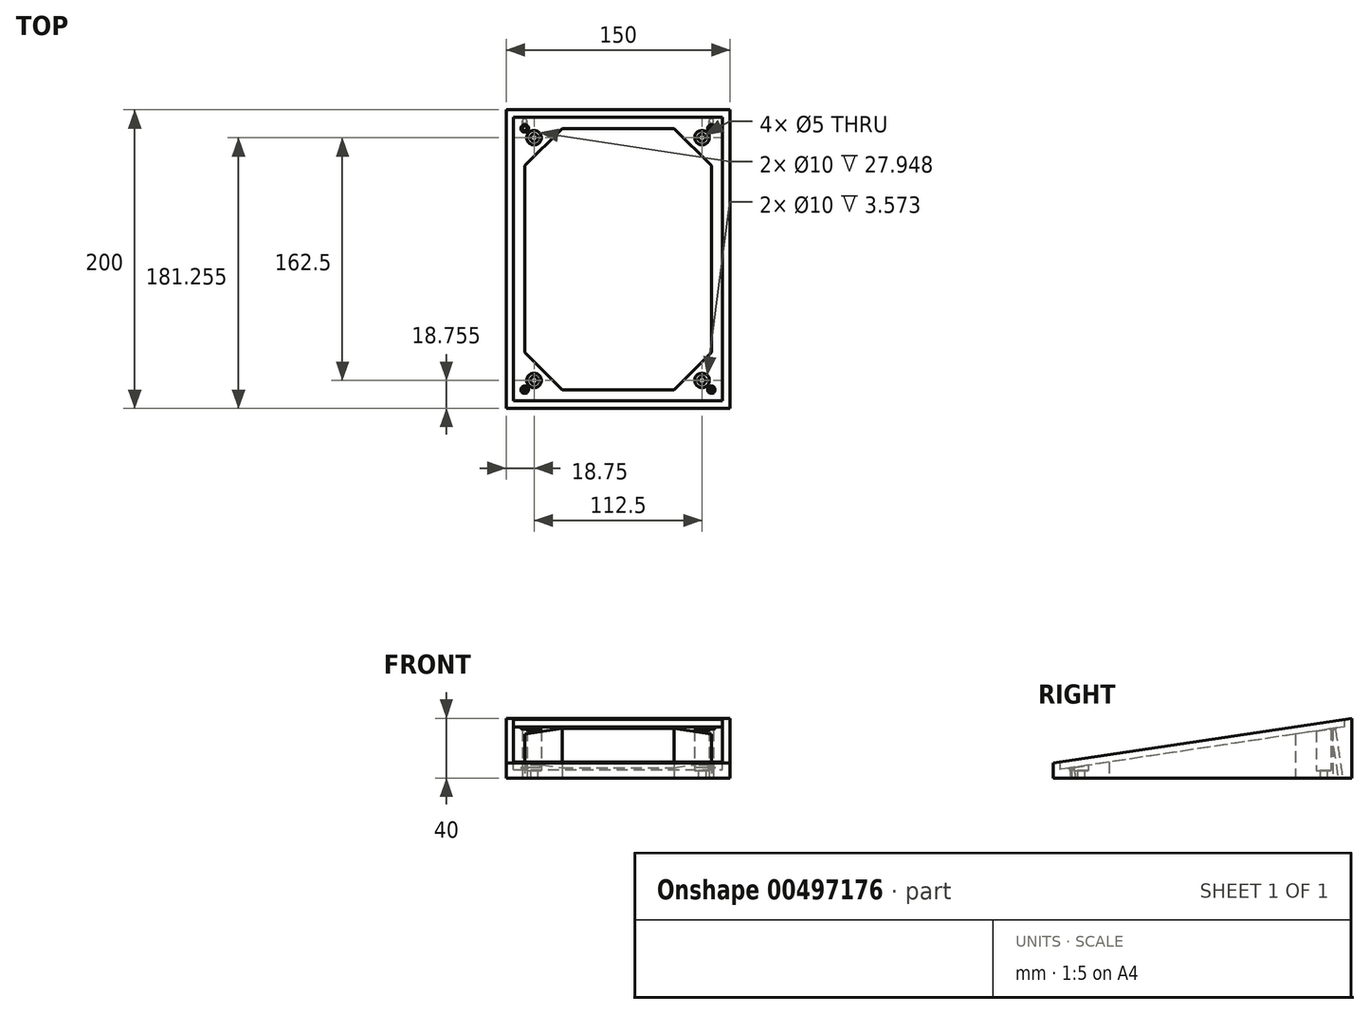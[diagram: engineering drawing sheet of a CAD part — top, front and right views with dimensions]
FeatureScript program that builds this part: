
annotation { "Feature Type Name" : "Feature", "Feature Type Description" : "" }
export const myFeature = defineFeature(function(context is Context, id is Id, definition is map)
    precondition{}
    {
        {
            var Q0;
            Q0=qCreatedBy(makeId("Top.planeOp"),FACE);
            var sketch = newSketch(context, id + "F0", { "sketchPlane" : qUnion([Q0])});
            skLineSegment(sketch, "E0.bottom", {"start": v(-75, 99.72) * mm, "end": v(75, 99.72) * mm});
            skLineSegment(sketch, "E0.top", {"start": v(-75, -100.28) * mm, "end": v(75, -100.28) * mm});
            skLineSegment(sketch, "E0.left", {"start": v(-75, 99.72) * mm, "end": v(-75, -100.28) * mm});
            skLineSegment(sketch, "E0.right", {"start": v(75, 99.72) * mm, "end": v(75, -100.28) * mm});
            skLineSegment(sketch, "E1.bottom", {"start": v(-68.75, 93.47) * mm, "end": v(68.75, 93.47) * mm});
            skLineSegment(sketch, "E1.top", {"start": v(-68.75, -94.03) * mm, "end": v(68.75, -94.03) * mm});
            skLineSegment(sketch, "E1.left", {"start": v(-68.75, 93.47) * mm, "end": v(-68.75, -94.03) * mm});
            skLineSegment(sketch, "E1.right", {"start": v(68.75, 93.47) * mm, "end": v(68.75, -94.03) * mm});
            skLineSegment(sketch, "E2.bottom", {"start": v(-62.5, 87.22) * mm, "end": v(62.5, 87.22) * mm});
            skLineSegment(sketch, "E2.top", {"start": v(-62.5, -87.78) * mm, "end": v(62.5, -87.78) * mm});
            skLineSegment(sketch, "E2.left", {"start": v(-62.5, 87.22) * mm, "end": v(-62.5, -87.78) * mm});
            skLineSegment(sketch, "E2.right", {"start": v(62.5, 87.22) * mm, "end": v(62.5, -87.78) * mm});
            skPoint(sketch, "E3", {"position": v(37.5, 87.22) * mm});
            skPoint(sketch, "E4", {"position": v(37.5, -87.78) * mm});
            skPoint(sketch, "E5", {"position": v(-37.5, 87.22) * mm});
            skPoint(sketch, "E6", {"position": v(-37.5, -87.78) * mm});
            skPoint(sketch, "E7", {"position": v(-62.5, 62.22) * mm});
            skPoint(sketch, "E8", {"position": v(62.5, 62.22) * mm});
            skPoint(sketch, "E9", {"position": v(62.5, -62.78) * mm});
            skPoint(sketch, "E10", {"position": v(-62.5, -62.78) * mm});
            skPoint(sketch, "E11", {"position": v(-62.5, 87.22) * mm});
            skPoint(sketch, "E12", {"position": v(62.5, 87.22) * mm});
            skPoint(sketch, "E13", {"position": v(62.5, -87.78) * mm});
            skPoint(sketch, "E14", {"position": v(-62.5, -87.78) * mm});
            skLineSegment(sketch, "E15", {"start": v(-62.5, -62.78) * mm, "end": v(-37.5, -87.78) * mm});
            skLineSegment(sketch, "E16", {"start": v(37.5, -87.78) * mm, "end": v(62.5, -62.78) * mm});
            skLineSegment(sketch, "E17", {"start": v(62.5, 62.22) * mm, "end": v(37.5, 87.22) * mm});
            skLineSegment(sketch, "E18", {"start": v(-37.5, 87.22) * mm, "end": v(-62.5, 62.22) * mm});
            skPoint(sketch, "E19", {"position": v(-50, 74.72) * mm});
            skPoint(sketch, "E20", {"position": v(50, 74.72) * mm});
            skPoint(sketch, "E21", {"position": v(50, -75.28) * mm});
            skPoint(sketch, "E22", {"position": v(-50, -75.28) * mm});
            skLineSegment(sketch, "E23", {"start": v(-62.5, 87.22) * mm, "end": v(-50, 74.72) * mm, "construction": true});
            skLineSegment(sketch, "E24", {"start": v(62.5, 87.22) * mm, "end": v(50, 74.72) * mm, "construction": true});
            skLineSegment(sketch, "E25", {"start": v(62.5, -87.78) * mm, "end": v(50, -75.28) * mm, "construction": true});
            skLineSegment(sketch, "E26", {"start": v(-62.5, -87.78) * mm, "end": v(-50, -75.28) * mm, "construction": true});
            skPoint(sketch, "E27", {"position": v(-56.25, 80.97) * mm});
            skPoint(sketch, "E28", {"position": v(56.25, 80.97) * mm});
            skPoint(sketch, "E29", {"position": v(56.25, -81.53) * mm});
            skPoint(sketch, "E30", {"position": v(-56.25, -81.53) * mm});
            skCircle(sketch, "E31", {"center": v(-56.25, -81.53) * mm, "radius": 2.5 * mm});
            skCircle(sketch, "E32", {"center": v(56.25, -81.53) * mm, "radius": 2.5 * mm});
            skCircle(sketch, "E33", {"center": v(56.25, 80.97) * mm, "radius": 2.5 * mm});
            skCircle(sketch, "E34", {"center": v(-56.25, 80.97) * mm, "radius": 2.5 * mm});
            skCircle(sketch, "E35", {"center": v(-56.25, 80.97) * mm, "radius": 5 * mm});
            skCircle(sketch, "E36", {"center": v(56.25, 80.97) * mm, "radius": 5 * mm});
            skCircle(sketch, "E37", {"center": v(-56.25, -81.53) * mm, "radius": 5 * mm});
            skCircle(sketch, "E38", {"center": v(56.25, -81.53) * mm, "radius": 5 * mm});
            skSolve(sketch);
        }
        {
            var Q0;
            Q0=makeQuery(id+"F0.imprint","IMPRINT",FACE,{"disambiguationData":[TD([[makeQuery(id+"F0.imprint","IMPRINT",EDGE,{"derivedFrom":sQuery(id+"F0.wireOp",EDGE,"E0.bottom")}),-1.0]])]});
            var Q1;
            Q1=makeQuery(id+"F0.imprint","IMPRINT",FACE,{"disambiguationData":[TD([[makeQuery(id+"F0.imprint","IMPRINT",EDGE,{"derivedFrom":sQuery(id+"F0.wireOp",EDGE,"E1.bottom")}),-1.0]])]});
            var Q2;
            {var subQ0=sQuery(id+"F0.wireOp",EDGE,"E17");Q2=makeQuery(id+"F0.imprint","IMPRINT",FACE,{"disambiguationData":[TD([[makeQuery(id+"F0.imprint","IMPRINT",EDGE,{"derivedFrom":subQ0}),-1.0]])]});}
            var Q3;
            {var subQ5=sQuery(id+"F0.wireOp",EDGE,"E18");Q3=makeQuery(id+"F0.imprint","IMPRINT",FACE,{"disambiguationData":[TD([[makeQuery(id+"F0.imprint","IMPRINT",EDGE,{"derivedFrom":subQ5}),-1.0]])]});}
            var Q4;
            {var subQ5=sQuery(id+"F0.wireOp",EDGE,"E15");Q4=makeQuery(id+"F0.imprint","IMPRINT",FACE,{"disambiguationData":[TD([[makeQuery(id+"F0.imprint","IMPRINT",EDGE,{"derivedFrom":subQ5}),-1.0]])]});}
            var Q5;
            {var subQ0=sQuery(id+"F0.wireOp",EDGE,"E16");Q5=makeQuery(id+"F0.imprint","IMPRINT",FACE,{"disambiguationData":[TD([[makeQuery(id+"F0.imprint","IMPRINT",EDGE,{"derivedFrom":subQ0}),-1.0]])]});}
            extrude(context, id + "F1", {"entities" : qUnion([Q0, Q1, Q2, Q3, Q4, Q5]), "depth" : 40 * mm});
        }
        {
            var Q0;
            Q0=makeQuery(id+"F1.opExtrude","SWEPT_FACE",FACE,{"disambiguationData":[OSD([sQuery(id+"F0.wireOp",EDGE,"E0.right")])]});
            var sketch = newSketch(context, id + "F2", { "sketchPlane" : qUnion([Q0])});
            skPoint(sketch, "E39", {"position": v(-100.28, 40) * mm});
            skPoint(sketch, "E40", {"position": v(99.72, 40) * mm});
            skPoint(sketch, "E41", {"position": v(-100.28, 10) * mm});
            skLineSegment(sketch, "E42", {"start": v(-100.28, 40) * mm, "end": v(99.72, 40) * mm});
            skLineSegment(sketch, "E43", {"start": v(-100.28, 40) * mm, "end": v(-100.28, 10) * mm});
            skLineSegment(sketch, "E44", {"start": v(-100.28, 10) * mm, "end": v(99.72, 40) * mm});
            skSolve(sketch);
        }
        {
            var Q0;
            Q0=makeQuery(id+"F2.imprint","IMPRINT",FACE,{"disambiguationData":[TD([[makeQuery(id+"F2.imprint","IMPRINT",EDGE,{"derivedFrom":sQuery(id+"F2.wireOp",EDGE,"E42")}),1.0]])]});
            extrude(context, id + "F3", {"entities" : qUnion([Q0]), "operationType" : NewBodyOperationType.REMOVE, "oppositeDirection" : true, "depth" : 155 * mm});
        }
        {
            var Q0;
            Q0=makeQuery(id+"F1.opExtrude","SWEPT_FACE",FACE,{"disambiguationData":[OSD([sQuery(id+"F0.wireOp",EDGE,"E0.right")])]});
            var sketch = newSketch(context, id + "F4", { "sketchPlane" : qUnion([Q0])});
            skPoint(sketch, "E45", {"position": v(94.72, 39.25) * mm});
            skPoint(sketch, "E46", {"position": v(99.72, 40) * mm});
            skPoint(sketch, "E47", {"position": v(-100.28, 10) * mm});
            skPoint(sketch, "E48", {"position": v(-95.28, 10.75) * mm});
            skPoint(sketch, "E49", {"position": v(-95.28, 5.75) * mm});
            skPoint(sketch, "E50", {"position": v(94.72, 34.25) * mm});
            skLineSegment(sketch, "E51", {"start": v(-95.28, 10.75) * mm, "end": v(94.72, 39.25) * mm});
            skLineSegment(sketch, "E52", {"start": v(94.72, 39.25) * mm, "end": v(94.72, 34.25) * mm});
            skLineSegment(sketch, "E53", {"start": v(94.72, 34.25) * mm, "end": v(-95.28, 5.75) * mm});
            skLineSegment(sketch, "E54", {"start": v(-95.28, 5.75) * mm, "end": v(-95.28, 10.75) * mm});
            skSolve(sketch);
        }
        {
            var Q0;
            Q0=makeQuery(id+"F4.imprint","IMPRINT",FACE,{"disambiguationData":[TD([[makeQuery(id+"F4.imprint","IMPRINT",EDGE,{"derivedFrom":sQuery(id+"F4.wireOp",EDGE,"E51")}),-1.0]])]});
            extrude(context, id + "F5", {"entities" : qUnion([Q0]), "operationType" : NewBodyOperationType.REMOVE, "oppositeDirection" : true, "depth" : 145 * mm, "hasSecondDirection" : true, "secondDirectionOppositeDirection" : true, "secondDirectionDepth" : 5 * mm});
        }
        {
            var Q0;
            Q0=makeQuery(id+"F0.imprint","IMPRINT",FACE,{"disambiguationData":[TD([[makeQuery(id+"F0.imprint","IMPRINT",EDGE,{"derivedFrom":sQuery(id+"F0.wireOp",EDGE,"E34")}),-1.0]])]});
            var Q1;
            Q1=makeQuery(id+"F0.imprint","IMPRINT",FACE,{"disambiguationData":[TD([[makeQuery(id+"F0.imprint","IMPRINT",EDGE,{"derivedFrom":sQuery(id+"F0.wireOp",EDGE,"E33")}),-1.0]])]});
            var Q2;
            Q2=makeQuery(id+"F0.imprint","IMPRINT",FACE,{"disambiguationData":[TD([[makeQuery(id+"F0.imprint","IMPRINT",EDGE,{"derivedFrom":sQuery(id+"F0.wireOp",EDGE,"E32")}),-1.0]])]});
            var Q3;
            Q3=makeQuery(id+"F0.imprint","IMPRINT",FACE,{"disambiguationData":[TD([[makeQuery(id+"F0.imprint","IMPRINT",EDGE,{"derivedFrom":sQuery(id+"F0.wireOp",EDGE,"E31")}),-1.0]])]});
            extrude(context, id + "F6", {"entities" : qUnion([Q0, Q1, Q2, Q3]), "operationType" : NewBodyOperationType.ADD, "depth" : 5 * mm});
        }
        {
            var Q0;
            Q0=makeQuery(id+"F5.boolean.opBoolean","COPY",FACE,{"derivedFrom":makeQuery(id+"F5.opExtrude","SWEPT_FACE",FACE,{"disambiguationData":[OSD([sQuery(id+"F4.wireOp",EDGE,"E53")])]})});
            var sketch = newSketch(context, id + "F7", { "sketchPlane" : qUnion([Q0])});
            skPoint(sketch, "E55", {"position": v(-56.25, 84.85) * mm});
            skPoint(sketch, "E56", {"position": v(56.25, 84.85) * mm});
            skPoint(sketch, "E57", {"position": v(56.25, -79.46) * mm});
            skPoint(sketch, "E58", {"position": v(-56.25, -79.46) * mm});
            skPoint(sketch, "E59", {"position": v(-62.5, 91.17) * mm});
            skPoint(sketch, "E60", {"position": v(62.5, 91.17) * mm});
            skPoint(sketch, "E61", {"position": v(62.5, -85.78) * mm});
            skPoint(sketch, "E62", {"position": v(-62.5, -85.78) * mm});
            skPoint(sketch, "E63", {"position": v(-70, -93.37) * mm});
            skPoint(sketch, "E64", {"position": v(-70, 98.76) * mm});
            skPoint(sketch, "E65", {"position": v(70, -93.37) * mm});
            skSolve(sketch);
        }
        {
            var Q0;
            Q0=sQuery(id+"F7.wireOp",VERTEX,"E62");
            var Q1;
            Q1=sQuery(id+"F7.wireOp",VERTEX,"E59");
            var Q2;
            Q2=sQuery(id+"F7.wireOp",VERTEX,"E60");
            var Q3;
            Q3=sQuery(id+"F7.wireOp",VERTEX,"E61");
            var Q4;
            Q4=makeQuery(id+"F1.opExtrude","SWEPT_BODY",BODY,{"disambiguationData":[OSD([sQuery(id+"F0.wireOp",EDGE,"E0.bottom"),sQuery(id+"F0.wireOp",EDGE,"E0.top"),sQuery(id+"F0.wireOp",EDGE,"E0.left"),sQuery(id+"F0.wireOp",EDGE,"E0.right"),sQuery(id+"F0.wireOp",EDGE,"E2.bottom"),sQuery(id+"F0.wireOp",EDGE,"E2.top"),sQuery(id+"F0.wireOp",EDGE,"E2.left"),sQuery(id+"F0.wireOp",EDGE,"E2.right"),sQuery(id+"F0.wireOp",EDGE,"E15"),sQuery(id+"F0.wireOp",EDGE,"E16"),sQuery(id+"F0.wireOp",EDGE,"E17"),sQuery(id+"F0.wireOp",EDGE,"E18"),sQuery(id+"F0.wireOp",EDGE,"E35"),sQuery(id+"F0.wireOp",EDGE,"E36"),sQuery(id+"F0.wireOp",EDGE,"E37"),sQuery(id+"F0.wireOp",EDGE,"E38")])]});
            hole(context, id + "F8", {"style" : HoleStyle.C_SINK, "endStyle" : HoleEndStyle.THROUGH, "holeDiameter" : 3 * mm, "cSinkDiameter" : 5 * mm, "cSinkAngle" : 90 * degree, "isTappedThrough" : true, "tappedDepth" : 12 * mm, "tapClearance" : 3, "locations" : qUnion([Q0, Q1, Q2, Q3]), "scope" : qUnion([Q4])});
        }
    });
